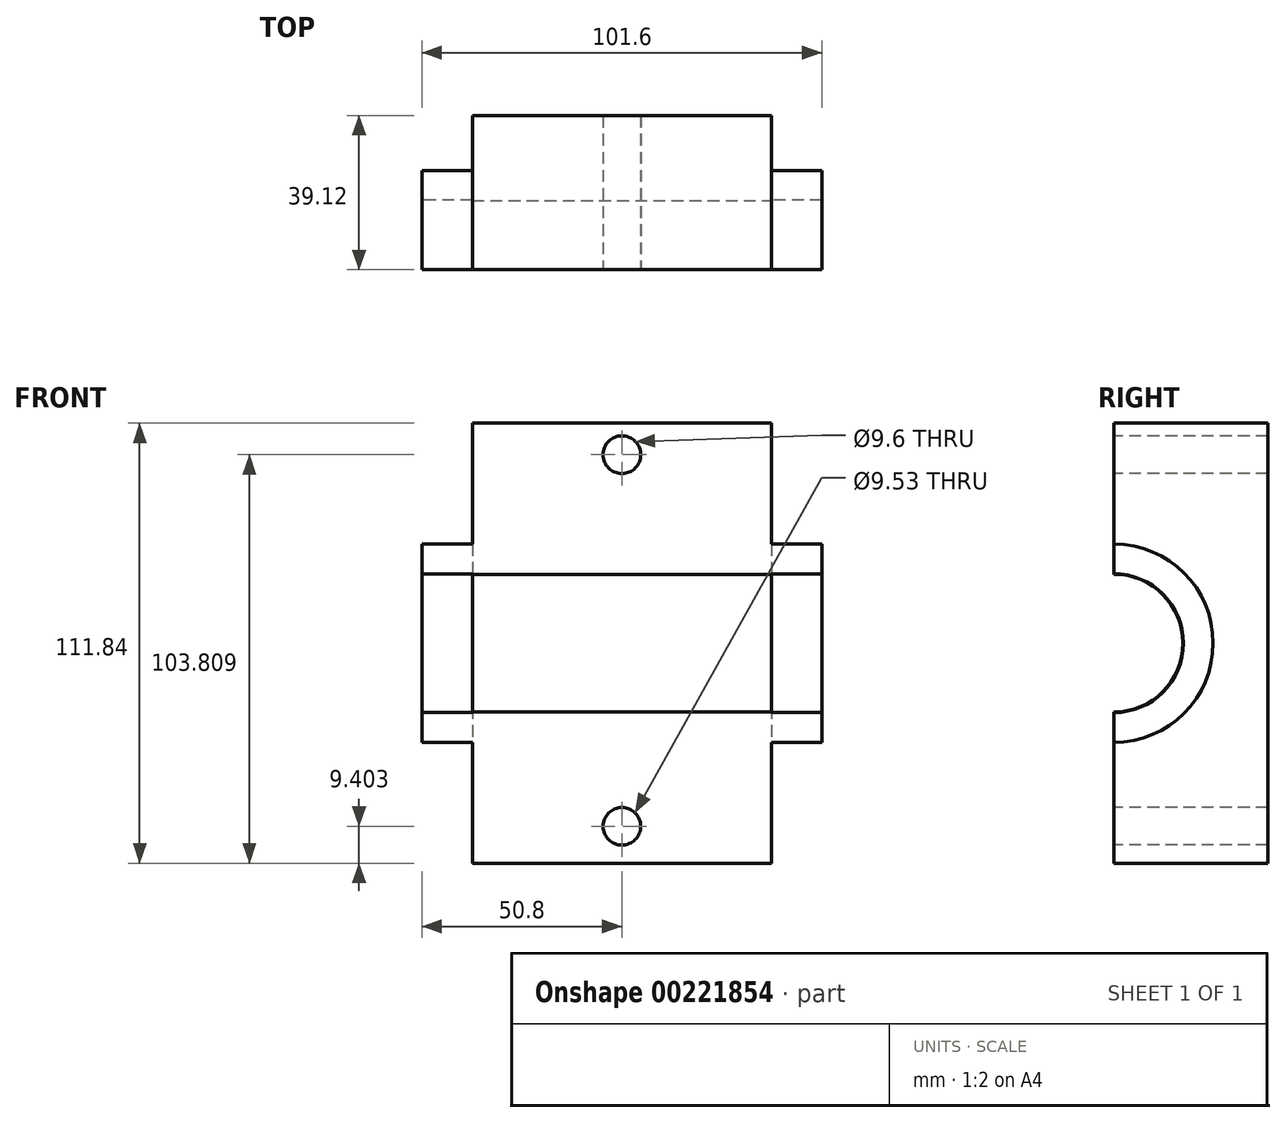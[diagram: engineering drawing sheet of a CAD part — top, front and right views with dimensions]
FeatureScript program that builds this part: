
annotation { "Feature Type Name" : "Feature", "Feature Type Description" : "" }
export const myFeature = defineFeature(function(context is Context, id is Id, definition is map)
    precondition{}
    {
        {
            var Q0;
            Q0=qCreatedBy(makeId("Front.planeOp"),FACE);
            var sketch = newSketch(context, id + "F0", { "sketchPlane" : qUnion([Q0])});
            skLineSegment(sketch, "E0.bottom", {"start": v(38, 55.92) * mm, "end": v(-38, 55.92) * mm});
            skLineSegment(sketch, "E0.top", {"start": v(38, -55.92) * mm, "end": v(-38, -55.92) * mm});
            skLineSegment(sketch, "E0.left", {"start": v(38, 55.92) * mm, "end": v(38, -55.92) * mm});
            skLineSegment(sketch, "E0.right", {"start": v(-38, 55.92) * mm, "end": v(-38, -55.92) * mm});
            skPoint(sketch, "E0.middle", {"position": v(0, 0) * mm});
            skCircle(sketch, "E1", {"center": v(0, 47.89) * mm, "radius": 4.8 * mm});
            skCircle(sketch, "E2", {"center": v(0, -46.52) * mm, "radius": 4.77 * mm});
            skPoint(sketch, "E2.centerSnap0", {"position": v(0, -55.92) * mm});
            skSolve(sketch);
        }
        {
            var Q0;
            Q0 = qSketchRegion(id + "F0", true);
            extrude(context, id + "F1", {"entities" : qUnion([Q0]), "oppositeDirection" : true, "depth" : 39.12 * mm});
        }
        {
            var Q0;
            Q0=qCreatedBy(makeId("Right.planeOp"),FACE);
            var sketch = newSketch(context, id + "F2", { "sketchPlane" : qUnion([Q0])});
            skCircle(sketch, "E3", {"center": v(0, 0) * mm, "radius": 25.2 * mm});
            skCircle(sketch, "E4", {"center": v(0, 0) * mm, "radius": 17.63 * mm});
            skSolve(sketch);
        }
        {
            var Q0;
            Q0=makeQuery(id+"F2.imprint","IMPRINT",FACE,{"disambiguationData":[TD([[makeQuery(id+"F2.imprint","IMPRINT",EDGE,{"derivedFrom":sQuery(id+"F2.wireOp",EDGE,"E3")}),1.0]])]});
            extrude(context, id + "F3", {"entities" : qUnion([Q0]), "operationType" : NewBodyOperationType.ADD, "depth" : 50.8 * mm, "hasSecondDirection" : true, "secondDirectionOppositeDirection" : true, "secondDirectionDepth" : 50.8 * mm});
        }
        {
            var Q0;
            Q0=qCreatedBy(makeId("Right.planeOp"),FACE);
            var sketch = newSketch(context, id + "F4", { "sketchPlane" : qUnion([Q0])});
            skCircle(sketch, "E5", {"center": v(0, 0) * mm, "radius": 17.5 * mm});
            skSolve(sketch);
        }
        {
            var Q0;
            Q0 = qSketchRegion(id + "F4", true);
            extrude(context, id + "F5", {"entities" : qUnion([Q0]), "operationType" : NewBodyOperationType.REMOVE, "oppositeDirection" : true, "depth" : 77.98 * mm, "hasSecondDirection" : true, "secondDirectionOppositeDirection" : false, "secondDirectionDepth" : 76.96 * mm});
        }
        {
            var Q0;
            Q0=qCreatedBy(makeId("Right.planeOp"),FACE);
            var sketch = newSketch(context, id + "F6", { "sketchPlane" : qUnion([Q0])});
            skLineSegment(sketch, "E6.bottom", {"start": v(-38.58, 25.56) * mm, "end": v(0, 25.56) * mm});
            skLineSegment(sketch, "E6.top", {"start": v(-38.58, -25.56) * mm, "end": v(0, -25.56) * mm});
            skLineSegment(sketch, "E6.left", {"start": v(-38.58, 25.56) * mm, "end": v(-38.58, -25.56) * mm});
            skLineSegment(sketch, "E6.right", {"start": v(0, 25.56) * mm, "end": v(0, -25.56) * mm});
            skSolve(sketch);
        }
        {
            var Q0;
            Q0 = qSketchRegion(id + "F6", true);
            extrude(context, id + "F7", {"entities" : qUnion([Q0]), "operationType" : NewBodyOperationType.REMOVE, "oppositeDirection" : true, "depth" : 50.8 * mm, "hasSecondDirection" : true, "secondDirectionOppositeDirection" : false, "secondDirectionDepth" : 50.8 * mm});
        }
    });
